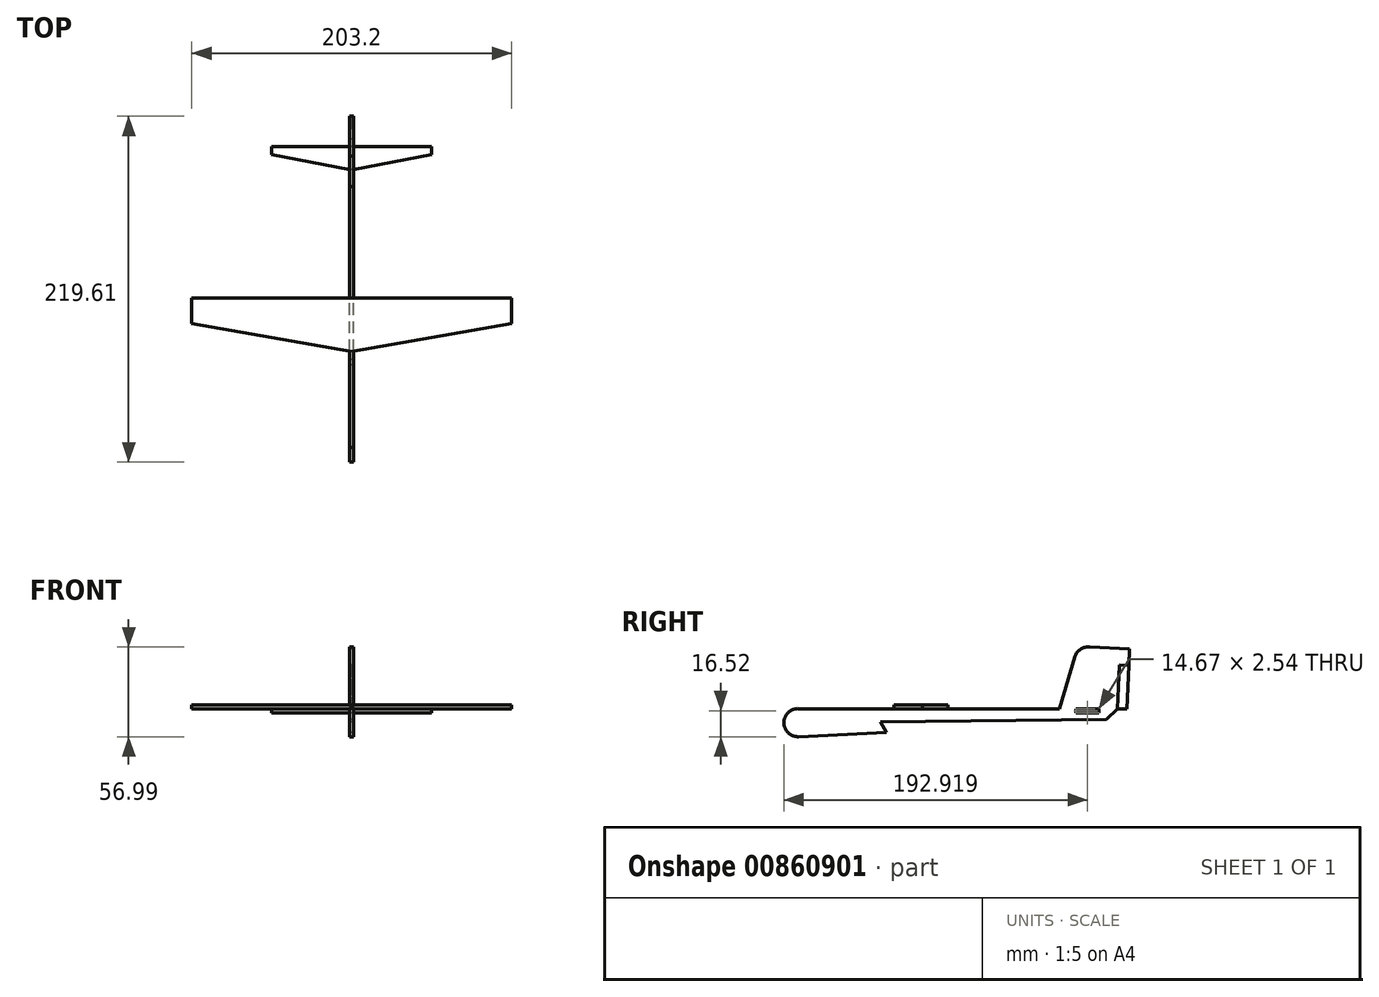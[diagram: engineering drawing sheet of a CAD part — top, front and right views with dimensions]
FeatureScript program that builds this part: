
annotation { "Feature Type Name" : "Feature", "Feature Type Description" : "" }
export const myFeature = defineFeature(function(context is Context, id is Id, definition is map)
    precondition{}
    {
        {
            var Q0;
            Q0=qCreatedBy(makeId("Right.planeOp"),FACE);
            var sketch = newSketch(context, id + "F0", { "sketchPlane" : qUnion([Q0])});
            skLineSegment(sketch, "E0", {"start": v(-101.3, 0) * mm, "end": v(64.46, 0) * mm});
            skLineSegment(sketch, "E1", {"start": v(-101.3, -17.78) * mm, "end": v(-45.52, -15.12) * mm});
            skLineSegment(sketch, "E2", {"start": v(-45.52, -15.12) * mm, "end": v(-49.07, -8.46) * mm});
            skLineSegment(sketch, "E3", {"start": v(-49.07, -8.46) * mm, "end": v(94.44, -6.69) * mm});
            skArc(sketch, "E4", {"start": v(-101.3, 0) * mm, "mid": v(-110.61, -8.89) * mm, "end": v(-101.3, -17.78) * mm});
            skLineSegment(sketch, "E5", {"start": v(109, 37.94) * mm, "end": v(107.26, 0) * mm});
            skLineSegment(sketch, "E6", {"start": v(107.26, 0) * mm, "end": v(101.33, 0) * mm});
            skLineSegment(sketch, "E7", {"start": v(101.33, 0) * mm, "end": v(102.6, 27.66) * mm});
            skLineSegment(sketch, "E8", {"start": v(109, 37.94) * mm, "end": v(83.8, 39.1) * mm});
            skArc(sketch, "E9", {"start": v(83.8, 39.1) * mm, "mid": v(77.99, 37.89) * mm, "end": v(74.4, 33.17) * mm});
            skLineSegment(sketch, "E10", {"start": v(74.4, 33.17) * mm, "end": v(64.46, 0) * mm});
            skLineSegment(sketch, "E11", {"start": v(102.6, 27.66) * mm, "end": v(108.52, 27.4) * mm});
            skLineSegment(sketch, "E12", {"start": v(94.44, -6.69) * mm, "end": v(101.33, 0) * mm});
            skPoint(sketch, "E13.orphan", {"position": v(101.33, -6.6) * mm});
            skLineSegment(sketch, "E14", {"start": v(74.97, 0) * mm, "end": v(89.64, 0) * mm});
            skLineSegment(sketch, "E15", {"start": v(74.97, 0) * mm, "end": v(74.97, -2.54) * mm});
            skLineSegment(sketch, "E16", {"start": v(74.97, -2.54) * mm, "end": v(89.64, -2.54) * mm});
            skLineSegment(sketch, "E17", {"start": v(89.64, -2.54) * mm, "end": v(89.64, 0) * mm});
            skSolve(sketch);
        }
        {
            var Q0;
            Q0=makeQuery(id+"F0.imprint","IMPRINT",FACE,{"disambiguationData":[TD([[makeQuery(id+"F0.imprint","IMPRINT",EDGE,{"derivedFrom":sQuery(id+"F0.wireOp",EDGE,"E0")}),-1.0]])]});
            extrude(context, id + "F1", {"entities" : qUnion([Q0]), "depth" : 1.27 * mm, "offsetDistance" : 25.4 * mm});
        }
        {
            var Q0;
            Q0=makeQuery(id+"F1.opExtrude","SWEPT_BODY",BODY,{"disambiguationData":[OSD([sQuery(id+"F0.wireOp",EDGE,"E0"),sQuery(id+"F0.wireOp",EDGE,"E1"),sQuery(id+"F0.wireOp",EDGE,"E2"),sQuery(id+"F0.wireOp",EDGE,"E3"),sQuery(id+"F0.wireOp",EDGE,"E4"),sQuery(id+"F0.wireOp",EDGE,"E5"),sQuery(id+"F0.wireOp",EDGE,"E7"),sQuery(id+"F0.wireOp",EDGE,"E8"),sQuery(id+"F0.wireOp",EDGE,"E9"),sQuery(id+"F0.wireOp",EDGE,"E10"),sQuery(id+"F0.wireOp",EDGE,"E11"),sQuery(id+"F0.wireOp",EDGE,"E12"),sQuery(id+"F0.wireOp",EDGE,"E14"),sQuery(id+"F0.wireOp",EDGE,"E15"),sQuery(id+"F0.wireOp",EDGE,"E16"),sQuery(id+"F0.wireOp",EDGE,"E17")])]});
            var Q1;
            Q1=qCreatedBy(makeId("Right.planeOp"),FACE);
            mirror(context, id + "F2", {"operationType" : NewBodyOperationType.ADD, "entities" : qUnion([Q0]), "mirrorPlane" : qUnion([Q1])});
        }
        {
            var Q0;
            Q0=makeQuery(id+"F1.opExtrude","SWEPT_FACE",FACE,{"disambiguationData":[OSD([sQuery(id+"F0.wireOp",EDGE,"E0")])]});
            var sketch = newSketch(context, id + "F3", { "sketchPlane" : qUnion([Q0])});
            skLineSegment(sketch, "E18", {"start": v(0, -6.33) * mm, "end": v(-101.6, -6.33) * mm});
            skLineSegment(sketch, "E19", {"start": v(-101.6, -6.33) * mm, "end": v(-101.6, -22.57) * mm});
            skLineSegment(sketch, "E20", {"start": v(-101.6, -22.57) * mm, "end": v(0, -40.48) * mm});
            skLineSegment(sketch, "E21.MirrorCS", {"start": v(101.6, -6.33) * mm, "end": v(101.6, -22.57) * mm});
            skLineSegment(sketch, "E22.MirrorCS", {"start": v(0, -6.33) * mm, "end": v(101.6, -6.33) * mm});
            skLineSegment(sketch, "E23.MirrorCS", {"start": v(101.6, -22.57) * mm, "end": v(0, -40.48) * mm});
            skSolve(sketch);
        }
        {
            var Q0;
            Q0 = qSketchRegion(id + "F3", true);
            extrude(context, id + "F4", {"entities" : qUnion([Q0]), "operationType" : NewBodyOperationType.ADD, "depth" : 2.54 * mm, "offsetDistance" : 25.4 * mm});
        }
        {
            var Q0;
            {var subQ0=sQuery(id+"F0.wireOp",EDGE,"E6");Q0=makeQuery(id+"F0.imprint","IMPRINT",FACE,{"disambiguationData":[TD([[makeQuery(id+"F0.imprint","IMPRINT",EDGE,{"derivedFrom":subQ0}),-1.0]])]});}
            extrude(context, id + "F5", {"entities" : qUnion([Q0]), "depth" : 0.64 * mm, "offsetDistance" : 25.4 * mm});
        }
        {
            var Q0;
            Q0=makeQuery(id+"F5.opExtrude","SWEPT_BODY",BODY,{"disambiguationData":[OSD([sQuery(id+"F0.wireOp",EDGE,"E5"),sQuery(id+"F0.wireOp",EDGE,"E6"),sQuery(id+"F0.wireOp",EDGE,"E7"),sQuery(id+"F0.wireOp",EDGE,"E11")])]});
            var Q1;
            Q1=qCreatedBy(makeId("Right.planeOp"),FACE);
            mirror(context, id + "F6", {"entities" : qUnion([Q0]), "mirrorPlane" : qUnion([Q1])});
        }
        {
            var Q0;
            {var subQ0=makeQuery(id+"F1.opExtrude","SWEPT_FACE",FACE,{"disambiguationData":[OSD([sQuery(id+"F0.wireOp",EDGE,"E16")])]});Q0=makeQuery(id+"F2.boolean.opBoolean","MERGE",FACE,{"derivedFrom":[subQ0,makeQuery(id+"F2.opPattern","COPY",FACE,{"derivedFrom":subQ0,"instanceName":"1"})]});}
            var sketch = newSketch(context, id + "F7", { "sketchPlane" : qUnion([Q0])});
            skLineSegment(sketch, "E24", {"start": v(17.45, 74.97) * mm, "end": v(-22.32, 74.97) * mm, "construction": true});
            skLineSegment(sketch, "E25", {"start": v(0, 89.64) * mm, "end": v(-50.8, 89.64) * mm});
            skLineSegment(sketch, "E26", {"start": v(0, 89.64) * mm, "end": v(50.8, 89.64) * mm});
            skLineSegment(sketch, "E27", {"start": v(-50.8, 89.64) * mm, "end": v(-50.8, 84.56) * mm});
            skLineSegment(sketch, "E28", {"start": v(-50.8, 84.56) * mm, "end": v(0, 74.97) * mm});
            skLineSegment(sketch, "E29", {"start": v(0, 74.97) * mm, "end": v(50.8, 84.56) * mm});
            skLineSegment(sketch, "E30", {"start": v(50.8, 84.56) * mm, "end": v(50.8, 89.64) * mm});
            skSolve(sketch);
        }
        {
            var Q0;
            {var subQ3=sQuery(id+"F7.wireOp",EDGE,"E30");Q0=makeQuery(id+"F7.imprint","IMPRINT",FACE,{"disambiguationData":[TD([[makeQuery(id+"F7.imprint","IMPRINT",EDGE,{"derivedFrom":subQ3}),1.0]])]});}
            var Q1;
            {var subQ3=sQuery(id+"F7.wireOp",EDGE,"E27");Q1=makeQuery(id+"F7.imprint","IMPRINT",FACE,{"disambiguationData":[TD([[makeQuery(id+"F7.imprint","IMPRINT",EDGE,{"derivedFrom":subQ3}),1.0]])]});}
            extrude(context, id + "F8", {"entities" : qUnion([Q0, Q1]), "depth" : 2.54 * mm, "offsetDistance" : 25.4 * mm});
        }
    });
